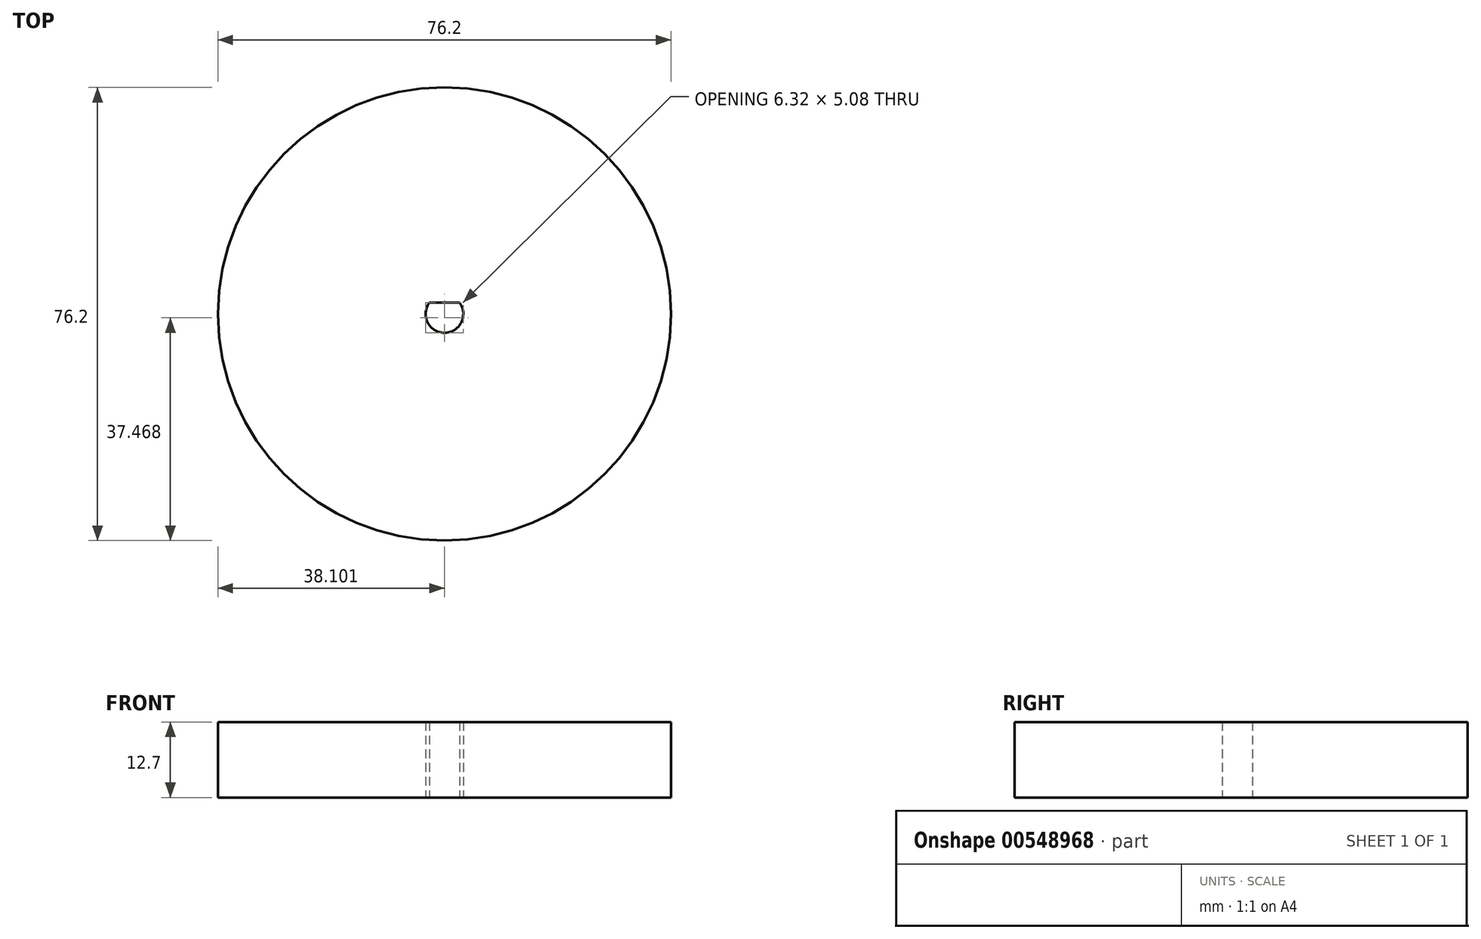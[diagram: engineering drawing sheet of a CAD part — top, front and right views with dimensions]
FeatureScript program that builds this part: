
annotation { "Feature Type Name" : "Feature", "Feature Type Description" : "" }
export const myFeature = defineFeature(function(context is Context, id is Id, definition is map)
    precondition{}
    {
        {
            var Q0;
            Q0=qCreatedBy(makeId("Top.planeOp"),FACE);
            var sketch = newSketch(context, id + "F0", { "sketchPlane" : qUnion([Q0])});
            skCircle(sketch, "E0", {"center": v(-84.73, -10.48) * mm, "radius": 38.1 * mm});
            skArc(sketch, "E1", {"start": v(-87.27, -8.57) * mm, "mid": v(-84.73, -13.65) * mm, "end": v(-82.19, -8.57) * mm});
            skLineSegment(sketch, "E2", {"start": v(-87.27, -8.57) * mm, "end": v(-82.19, -8.57) * mm});
            skSolve(sketch);
        }
        {
            var Q0;
            Q0=makeQuery(id+"F0.imprint","IMPRINT",FACE,{"disambiguationData":[TD([[makeQuery(id+"F0.imprint","IMPRINT",EDGE,{"derivedFrom":sQuery(id+"F0.wireOp",EDGE,"E0")}),1.0]])]});
            extrude(context, id + "F1", {"entities" : qUnion([Q0]), "depth" : 12.7 * mm, "offsetDistance" : 25.4 * mm});
        }
    });
